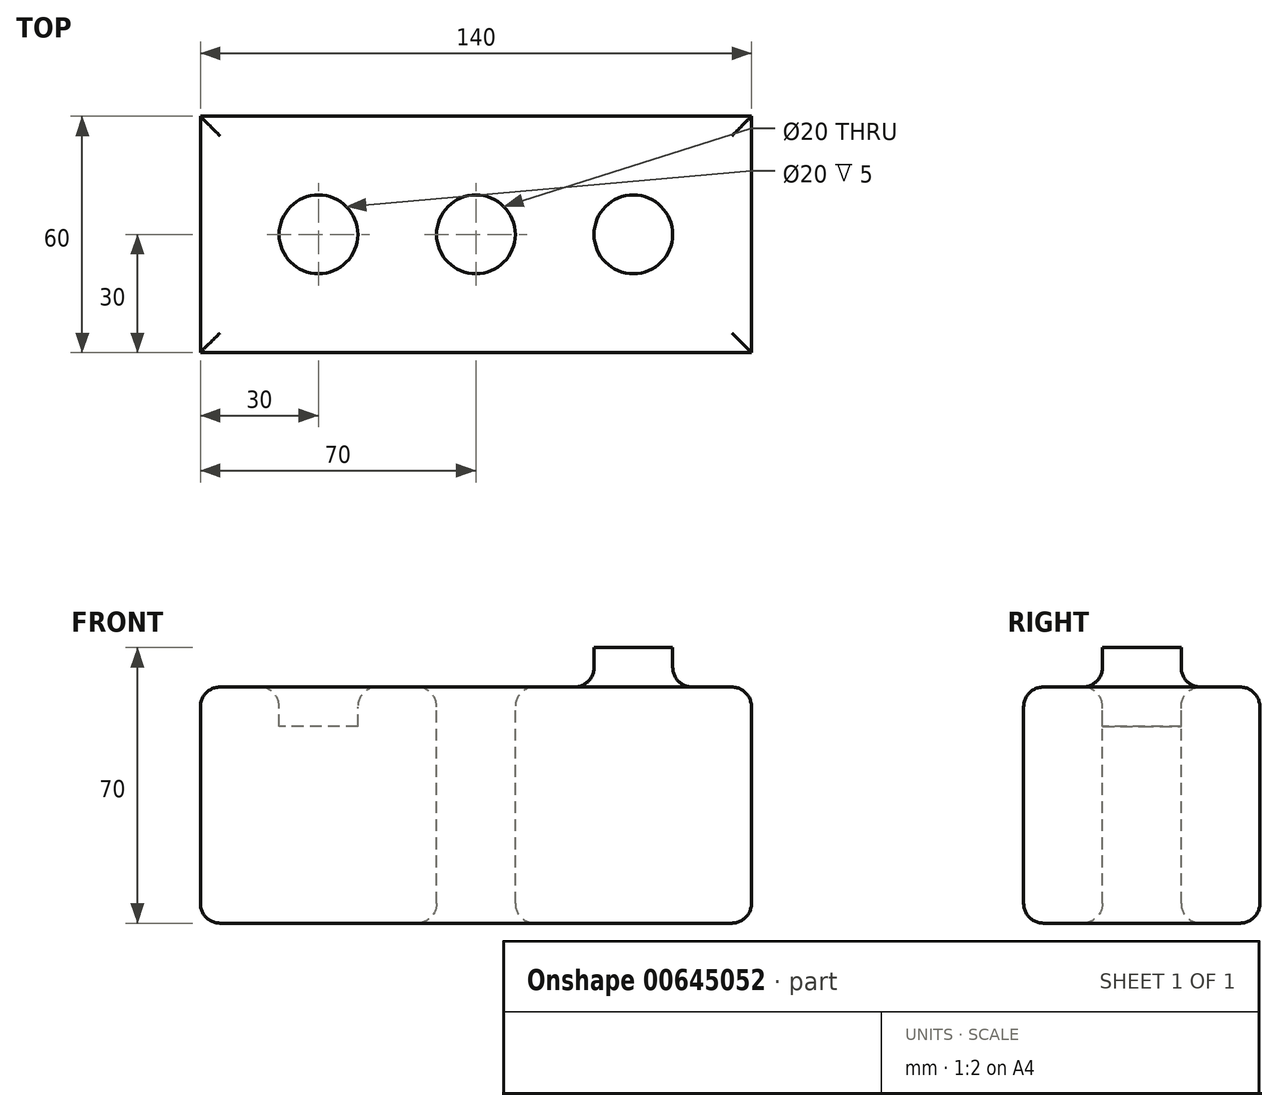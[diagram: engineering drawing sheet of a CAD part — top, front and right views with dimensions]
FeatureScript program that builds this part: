
annotation { "Feature Type Name" : "Feature", "Feature Type Description" : "" }
export const myFeature = defineFeature(function(context is Context, id is Id, definition is map)
    precondition{}
    {
        {
            var Q0;
            Q0=qCreatedBy(makeId("Top.planeOp"),FACE);
            var sketch = newSketch(context, id + "F0", { "sketchPlane" : qUnion([Q0])});
            skLineSegment(sketch, "E0.bottom", {"start": v(70, -30) * mm, "end": v(-70, -30) * mm});
            skLineSegment(sketch, "E0.top", {"start": v(70, 30) * mm, "end": v(-70, 30) * mm});
            skLineSegment(sketch, "E0.left", {"start": v(70, -30) * mm, "end": v(70, 30) * mm});
            skLineSegment(sketch, "E0.right", {"start": v(-70, -30) * mm, "end": v(-70, 30) * mm});
            skPoint(sketch, "E0.middle", {"position": v(0, 0) * mm});
            skSolve(sketch);
        }
        {
            var Q0;
            Q0 = qSketchRegion(id + "F0", true);
            extrude(context, id + "F1", {"entities" : qUnion([Q0]), "depth" : 60 * mm, "offsetDistance" : 25 * mm});
        }
        {
            var Q0;
            Q0=makeQuery(id+"F1.opExtrude","CAP_FACE",FACE,{"disambiguationData":[OSD([sQuery(id+"F0.wireOp",EDGE,"E0.bottom"),sQuery(id+"F0.wireOp",EDGE,"E0.top"),sQuery(id+"F0.wireOp",EDGE,"E0.left"),sQuery(id+"F0.wireOp",EDGE,"E0.right")])],"isStart":false});
            var sketch = newSketch(context, id + "F2", { "sketchPlane" : qUnion([Q0])});
            skCircle(sketch, "E1", {"center": v(-40, 0) * mm, "radius": 10 * mm});
            skSolve(sketch);
        }
        {
            var Q0;
            Q0=makeQuery(id+"F2.imprint","IMPRINT",FACE,{"disambiguationData":[TD([[makeQuery(id+"F2.imprint","IMPRINT",EDGE,{"derivedFrom":sQuery(id+"F2.wireOp",EDGE,"E1")}),-1.0]])]});
            var sketch = newSketch(context, id + "F3", { "sketchPlane" : qUnion([Q0])});
            skCircle(sketch, "E2", {"center": v(40, 0) * mm, "radius": 10 * mm});
            skSolve(sketch);
        }
        {
            var Q0;
            Q0=makeQuery(id+"F2.imprint","IMPRINT",FACE,{"disambiguationData":[TD([[makeQuery(id+"F2.imprint","IMPRINT",EDGE,{"derivedFrom":sQuery(id+"F2.wireOp",EDGE,"E1")}),-1.0]])]});
            var sketch = newSketch(context, id + "F4", { "sketchPlane" : qUnion([Q0])});
            skCircle(sketch, "E3", {"center": v(0, 0) * mm, "radius": 10 * mm});
            skSolve(sketch);
        }
        {
            var Q0;
            Q0 = qSketchRegion(id + "F3", true);
            extrude(context, id + "F5", {"entities" : qUnion([Q0]), "operationType" : NewBodyOperationType.ADD, "depth" : 10 * mm, "offsetDistance" : 25 * mm});
        }
        {
            var Q0;
            Q0 = qSketchRegion(id + "F4", true);
            extrude(context, id + "F6", {"entities" : qUnion([Q0]), "operationType" : NewBodyOperationType.REMOVE, "oppositeDirection" : true, "depth" : 96.3 * mm, "offsetDistance" : 25 * mm});
        }
        {
            var Q0;
            Q0=makeQuery(id+"F1.opExtrude","CAP_FACE",FACE,{"disambiguationData":[OSD([sQuery(id+"F0.wireOp",EDGE,"E0.bottom"),sQuery(id+"F0.wireOp",EDGE,"E0.top"),sQuery(id+"F0.wireOp",EDGE,"E0.left"),sQuery(id+"F0.wireOp",EDGE,"E0.right")])],"isStart":true});
            fillet(context, id + "F7", {"entities" : qUnion([Q0]), "radius" : 5 * mm, "tangentPropagation" : true, "allowEdgeOverflow" : false});
        }
        {
            var Q0;
            Q0 = qSketchRegion(id + "F2", true);
            extrude(context, id + "F8", {"entities" : qUnion([Q0]), "operationType" : NewBodyOperationType.REMOVE, "oppositeDirection" : true, "depth" : 10 * mm, "offsetDistance" : 25 * mm});
        }
        {
            var Q0;
            Q0=makeQuery(id+"F1.opExtrude","CAP_FACE",FACE,{"disambiguationData":[OSD([sQuery(id+"F0.wireOp",EDGE,"E0.bottom"),sQuery(id+"F0.wireOp",EDGE,"E0.top"),sQuery(id+"F0.wireOp",EDGE,"E0.left"),sQuery(id+"F0.wireOp",EDGE,"E0.right")])],"isStart":false});
            fillet(context, id + "F9", {"entities" : qUnion([Q0]), "radius" : 5 * mm, "tangentPropagation" : true, "allowEdgeOverflow" : false});
        }
    });
